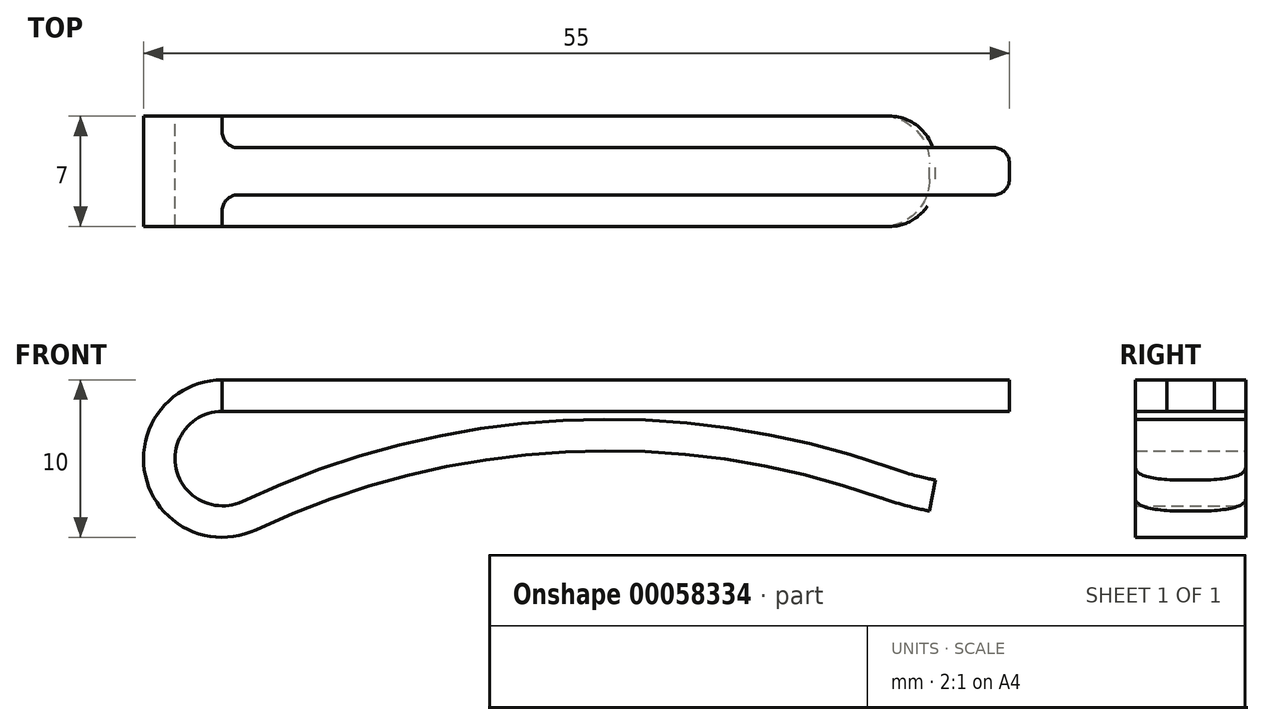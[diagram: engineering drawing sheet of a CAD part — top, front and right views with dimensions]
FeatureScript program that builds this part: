
annotation { "Feature Type Name" : "Feature", "Feature Type Description" : "" }
export const myFeature = defineFeature(function(context is Context, id is Id, definition is map)
    precondition{}
    {
        {
            var Q0;
            Q0=qCreatedBy(makeId("Front.planeOp"),FACE);
            var sketch = newSketch(context, id + "F0", { "sketchPlane" : qUnion([Q0])});
            skLineSegment(sketch, "E0", {"start": v(0, 0) * mm, "end": v(50, 0) * mm});
            skArc(sketch, "E1", {"start": v(0, 0) * mm, "mid": v(-2.93, -3.66) * mm, "end": v(1.28, -5.71) * mm});
            skArc(sketch, "E2", {"start": v(42.51, -3.6) * mm, "mid": v(21.7, -0.57) * mm, "end": v(1.28, -5.71) * mm});
            skArc(sketch, "E3", {"start": v(42.51, -3.6) * mm, "mid": v(43.9, -4.04) * mm, "end": v(45.3, -4.37) * mm});
            skLineSegment(sketch, "E4.0", {"start": v(0, 2) * mm, "end": v(50, 2) * mm});
            skArc(sketch, "E4.1", {"start": v(0, 2) * mm, "mid": v(-4.88, -4.1) * mm, "end": v(2.14, -7.52) * mm});
            skArc(sketch, "E4.2", {"start": v(41.85, -5.5) * mm, "mid": v(21.8, -2.57) * mm, "end": v(2.14, -7.52) * mm});
            skArc(sketch, "E4.3", {"start": v(41.85, -5.5) * mm, "mid": v(43.37, -5.97) * mm, "end": v(44.93, -6.33) * mm});
            skLineSegment(sketch, "E5", {"start": v(50, 2) * mm, "end": v(50, 0) * mm});
            skLineSegment(sketch, "E6", {"start": v(45.3, -4.37) * mm, "end": v(44.93, -6.33) * mm});
            skSolve(sketch);
        }
        {
            var Q0;
            Q0 = qSketchRegion(id + "F0", true);
            extrude(context, id + "F1", {"entities" : qUnion([Q0]), "depth" : 7 * mm});
        }
        {
            var Q0;
            Q0=makeQuery(id+"F1.opExtrude","SWEPT_FACE",FACE,{"disambiguationData":[OSD([sQuery(id+"F0.wireOp",EDGE,"E4.0")])]});
            var sketch = newSketch(context, id + "F2", { "sketchPlane" : qUnion([Q0])});
            skArc(sketch, "E7", {"start": v(43.9, -6.88) * mm, "mid": v(44.45, -6.97) * mm, "end": v(45, -7) * mm});
            skArc(sketch, "E8", {"start": v(43.9, -6.88) * mm, "mid": v(31.26, -5.19) * mm, "end": v(18.52, -5.76) * mm});
            skArc(sketch, "E9", {"start": v(0, -7) * mm, "mid": v(9.28, -6.69) * mm, "end": v(18.52, -5.76) * mm});
            skLineSegment(sketch, "E10", {"start": v(0, -7) * mm, "end": v(45, -7) * mm});
            skSolve(sketch);
        }
        {
            var Q0;
            Q0=makeQuery(id+"F1.opExtrude","SWEPT_FACE",FACE,{"disambiguationData":[OSD([sQuery(id+"F0.wireOp",EDGE,"E4.0")])]});
            var sketch = newSketch(context, id + "F3", { "sketchPlane" : qUnion([Q0])});
            skLineSegment(sketch, "E11", {"start": v(941.92, -2) * mm, "end": v(0, -2) * mm});
            skLineSegment(sketch, "E12", {"start": v(0, -5) * mm, "end": v(0, -7) * mm});
            skLineSegment(sketch, "E13", {"start": v(0, -5) * mm, "end": v(941.92, -5) * mm});
            skLineSegment(sketch, "E14", {"start": v(0, -2) * mm, "end": v(0, 0) * mm});
            skLineSegment(sketch, "E15", {"start": v(0, 0) * mm, "end": v(50, 0) * mm});
            skLineSegment(sketch, "E16", {"start": v(50, 0) * mm, "end": v(941.92, -2) * mm});
            skLineSegment(sketch, "E17", {"start": v(0.14, -8.55) * mm, "end": v(941.92, -6.97) * mm});
            skPoint(sketch, "E17.endSnap0", {"position": v(1.95, -6.97) * mm});
            skLineSegment(sketch, "E18", {"start": v(941.92, -6.97) * mm, "end": v(941.92, -5) * mm});
            skPoint(sketch, "E19.orphan", {"position": v(3.9, -6.95) * mm});
            skLineSegment(sketch, "E20", {"start": v(0, -7) * mm, "end": v(0.14, -8.55) * mm});
            skSolve(sketch);
        }
        {
            var Q0;
            Q0 = qSketchRegion(id + "F3", true);
            extrude(context, id + "F4", {"entities" : qUnion([Q0]), "operationType" : NewBodyOperationType.REMOVE, "oppositeDirection" : true, "depth" : 2 * mm});
        }
        {
            var Q0;
            Q0=makeQuery(id+"F4.boolean.opBoolean","COPY",EDGE,{"derivedFrom":makeQuery(id+"F4.opExtrude","SWEPT_EDGE",EDGE,{"disambiguationData":[OSD([sQuery(id+"F0.wireOp",EDGE,"E4.0"),sQuery(id+"F0.wireOp",EDGE,"E4.1"),sQuery(id+"F3.wireOp",EDGE,"E11"),sQuery(id+"F3.wireOp",EDGE,"E12")])]})});
            var Q1;
            {var subQ0=sQuery(id+"F2.wireOp",EDGE,"E9");Q1=makeQuery(id+"F4.boolean.opBoolean","MERGE",EDGE,{"derivedFrom":[makeQuery(id+"FFn8H8OMSKrgj5N_1.boolean.opBoolean","COPY",EDGE,{"disambiguationData":[OD(0.0)],"derivedFrom":makeQuery(id+"FFn8H8OMSKrgj5N_1.opExtrude","SWEPT_EDGE",EDGE,{"disambiguationData":[OSD([sQuery(id+"F0.wireOp",EDGE,"E4.0"),sQuery(id+"F0.wireOp",EDGE,"E4.1"),subQ0,sQuery(id+"F2.wireOp",EDGE,"E10")])]})}),makeQuery(id+"F4.opExtrude","SWEPT_EDGE",EDGE,{"disambiguationData":[OSD([subQ0,sQuery(id+"F3.wireOp",EDGE,"E12"),sQuery(id+"F3.wireOp",EDGE,"E13")])]})]});}
            var Q2;
            Q2=makeQuery(id+"F4.boolean.opBoolean","INTERSECT",EDGE,{"derivedFrom":[makeQuery(id+"F1.opExtrude","SWEPT_FACE",FACE,{"disambiguationData":[OSD([sQuery(id+"F0.wireOp",EDGE,"E5")])]}),makeQuery(id+"F4.opExtrude","SWEPT_FACE",FACE,{"disambiguationData":[OSD([sQuery(id+"F3.wireOp",EDGE,"E13")])]})]});
            var Q3;
            Q3=makeQuery(id+"F4.boolean.opBoolean","INTERSECT",EDGE,{"derivedFrom":[makeQuery(id+"F1.opExtrude","SWEPT_FACE",FACE,{"disambiguationData":[OSD([sQuery(id+"F0.wireOp",EDGE,"E5")])]}),makeQuery(id+"F4.opExtrude","SWEPT_FACE",FACE,{"disambiguationData":[OSD([sQuery(id+"F3.wireOp",EDGE,"E11")])]})]});
            var Q4;
            Q4=makeQuery(id+"F4.boolean.opBoolean","COPY",EDGE,{"derivedFrom":makeQuery(id+"F4.opExtrude","SWEPT_EDGE",EDGE,{"disambiguationData":[OSD([sQuery(id+"F0.wireOp",EDGE,"E4.0"),sQuery(id+"F3.wireOp",EDGE,"E12"),sQuery(id+"F3.wireOp",EDGE,"E20")])]})});
            var Q5;
            Q5=makeQuery(id+"F4.boolean.opBoolean","COPY",EDGE,{"derivedFrom":makeQuery(id+"F4.opExtrude","SWEPT_EDGE",EDGE,{"disambiguationData":[OSD([sQuery(id+"F3.wireOp",EDGE,"E14"),sQuery(id+"F3.wireOp",EDGE,"E15")])]})});
            fillet(context, id + "F5", {"entities" : qUnion([Q0, Q1, Q2, Q3, Q4, Q5]), "radius" : 1 * mm, "tangentPropagation" : true, "allowEdgeOverflow" : false});
        }
        {
            var Q0;
            Q0=makeQuery(id+"F1.opExtrude","CAP_EDGE",EDGE,{"disambiguationData":[OSD([sQuery(id+"F0.wireOp",EDGE,"E6")])],"isStart":false});
            var Q1;
            Q1=makeQuery(id+"F1.opExtrude","CAP_EDGE",EDGE,{"disambiguationData":[OSD([sQuery(id+"F0.wireOp",EDGE,"E6")])],"isStart":true});
            fillet(context, id + "F6", {"entities" : qUnion([Q0, Q1]), "radius" : 3 * mm, "tangentPropagation" : true, "allowEdgeOverflow" : false});
        }
    });
